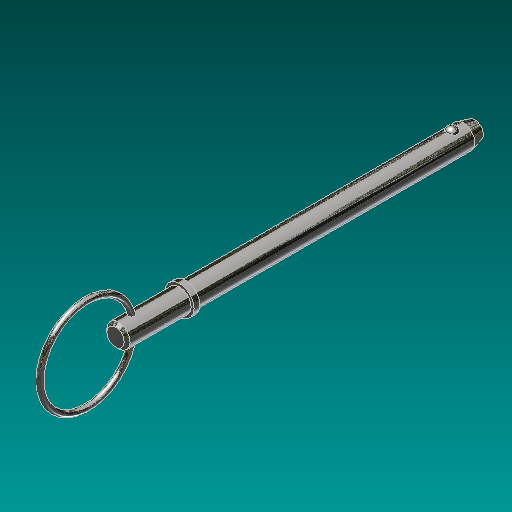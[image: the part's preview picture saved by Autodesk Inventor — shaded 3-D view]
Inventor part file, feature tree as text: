
AUTODESK INVENTOR PART (.ipt)
format: ipt  version: 2017 (Build 210142000, 142)  size: 153,088 bytes
history: native  units: in
note: dims shown in document units (in); Inventor stores cm internally (conversion verified against a paired STEP export)
features: sketch x5, extrude x2, chamfer x2, revolve x1, sweep x1
ambient origin geometry x8: Origin, YZ Plane, XZ Plane, XY Plane, X Axis, Y Axis, Z Axis, Center Point
bodies: Solid1 (feature_tree)
feature tree (11):
  extrude  "Extrusion1"  Depth=0.75in TaperAngle=0.0deg
  extrude  "Extrusion2"  Depth=0.0625in TaperAngle=0.0deg
  chamfer  "Chamfer1"  Distance=0.125in Angle=15.0deg
  chamfer  "Chamfer2"  Distance=0.0312in Angle=15.0deg
  revolve  "Revolution1"  [1 undecoded]
  sweep  "Sweep1"
  sketch  "Sketch1"  dims[d0=0.25in d1=0.75in d2=3.1125in d3=0.0in d4=0.0in]
  sketch  "Sketch2"  dims[d5=0.3125in d6=0.0625in d7=0.0in d8=0.125in d9=0.125in d10=15.0deg d11=0.0312in d12=0.125in d13=15.0deg]
  sketch  "Sketch3"  dims[d14=0.125in d15=2.8in]
  sketch  "Sketch4"  dims[d16=0.16in d17=90.0deg]
  sketch  "Sketch5"  dims[d18=1.0in d19=1.0625in d20=0.0625in d21=0.0in d22=0.0in]
note: 1 required parameter value undecoded (feature->parameter linkage not recoverable at this tier; creation-order binding heuristic only, values carry confidence <= 0.55)
